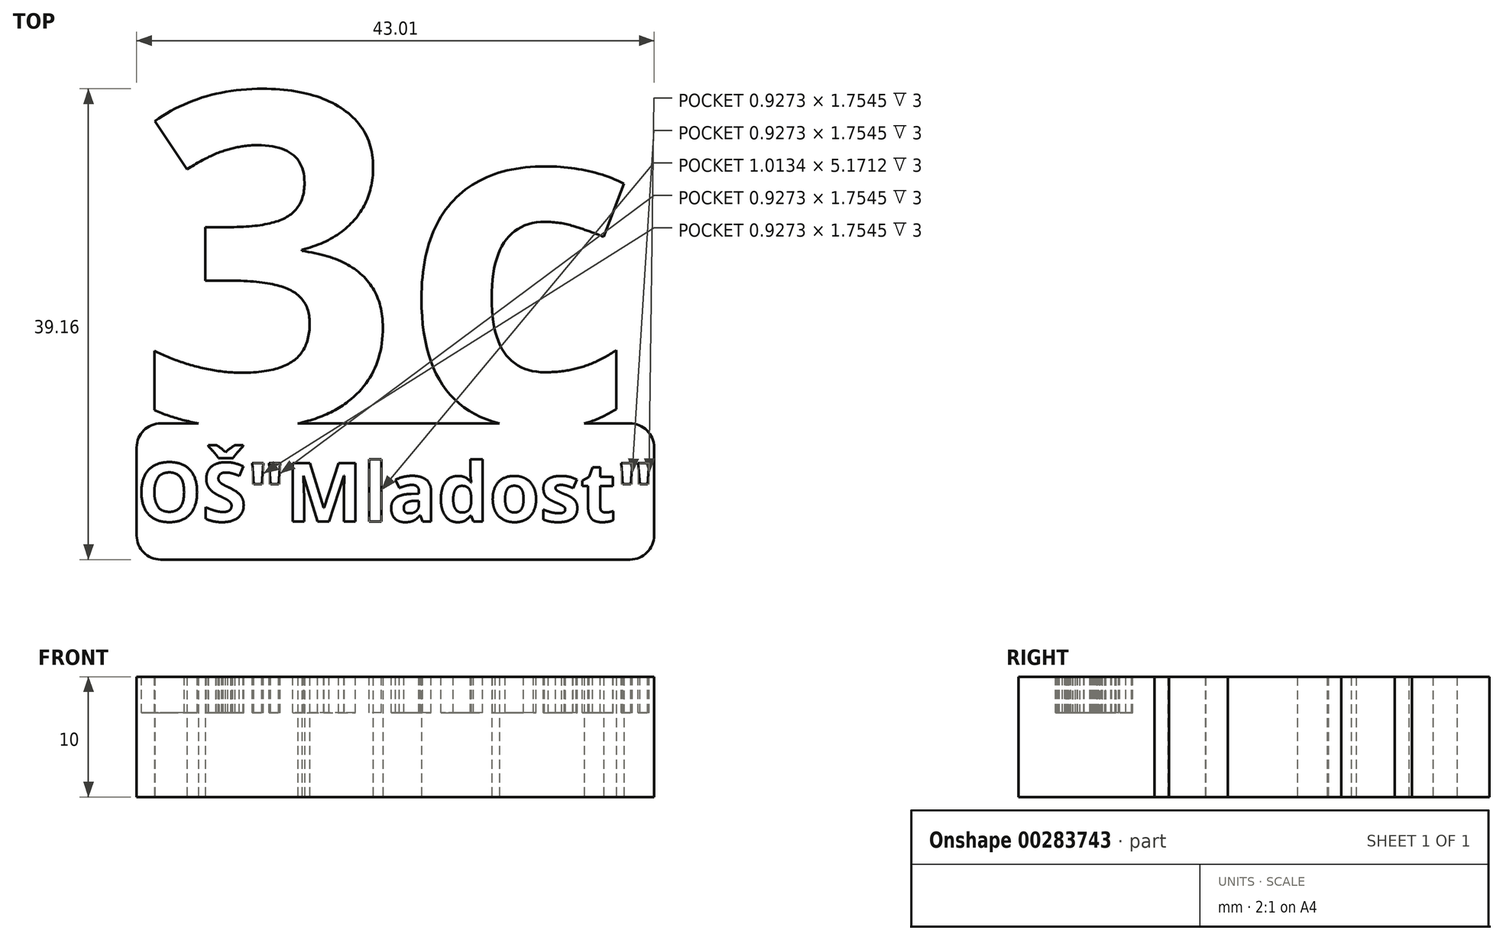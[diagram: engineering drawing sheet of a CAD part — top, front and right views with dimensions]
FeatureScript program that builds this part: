
annotation { "Feature Type Name" : "Feature", "Feature Type Description" : "" }
export const myFeature = defineFeature(function(context is Context, id is Id, definition is map)
    precondition{}
    {
        {
            var Q0;
            Q0=qCreatedBy(makeId("Top.planeOp"),FACE);
            var sketch = newSketch(context, id + "F0", { "sketchPlane" : qUnion([Q0])});
            skText(sketch, "E0", { "text": "3c", "fontName": "OpenSans-Bold.ttf"});
            skLineSegment(sketch, "E1.bottom", {"start": v(0, 0) * mm, "end": v(43, 0) * mm});
            skLineSegment(sketch, "E1.top", {"start": v(0, -11.32) * mm, "end": v(43, -11.32) * mm});
            skLineSegment(sketch, "E1.left", {"start": v(0, 0) * mm, "end": v(0, -11.32) * mm});
            skLineSegment(sketch, "E1.right", {"start": v(43, 0) * mm, "end": v(43, -11.32) * mm});
            const initialGuessF0  = {"E0": [0, 0, 1, 0, 0.02768]};
            skSetInitialGuess(sketch, initialGuessF0);
            skSolve(sketch);
        }
        {
            var Q0;
            Q0 = qSketchRegion(id + "F0", true);
            extrude(context, id + "F1", {"entities" : qUnion([Q0]), "depth" : 10 * mm});
        }
        {
            var Q0;
            Q0=makeQuery(id+"F1.opExtrude","CAP_FACE",FACE,{"disambiguationData":[OSD([sQuery(id+"F0.wireOp",EDGE,"E0.sketch_text.stroke-0"),sQuery(id+"F0.wireOp",EDGE,"E0.sketch_text.stroke-1"),sQuery(id+"F0.wireOp",EDGE,"E0.sketch_text.stroke-2"),sQuery(id+"F0.wireOp",EDGE,"E0.sketch_text.stroke-3"),sQuery(id+"F0.wireOp",EDGE,"E0.sketch_text.stroke-4"),sQuery(id+"F0.wireOp",EDGE,"E0.sketch_text.stroke-5"),sQuery(id+"F0.wireOp",EDGE,"E0.sketch_text.stroke-6"),sQuery(id+"F0.wireOp",EDGE,"E0.sketch_text.stroke-7"),sQuery(id+"F0.wireOp",EDGE,"E0.sketch_text.stroke-8"),sQuery(id+"F0.wireOp",EDGE,"E0.sketch_text.stroke-9"),sQuery(id+"F0.wireOp",EDGE,"E0.sketch_text.stroke-10"),sQuery(id+"F0.wireOp",EDGE,"E0.sketch_text.stroke-11"),sQuery(id+"F0.wireOp",EDGE,"E0.sketch_text.stroke-12"),sQuery(id+"F0.wireOp",EDGE,"E0.sketch_text.stroke-13"),sQuery(id+"F0.wireOp",EDGE,"E0.sketch_text.stroke-14"),sQuery(id+"F0.wireOp",EDGE,"E0.sketch_text.stroke-15"),sQuery(id+"F0.wireOp",EDGE,"E0.sketch_text.stroke-16"),sQuery(id+"F0.wireOp",EDGE,"E0.sketch_text.stroke-17"),sQuery(id+"F0.wireOp",EDGE,"E0.sketch_text.stroke-18"),sQuery(id+"F0.wireOp",EDGE,"E0.sketch_text.stroke-19"),sQuery(id+"F0.wireOp",EDGE,"E0.sketch_text.stroke-20"),sQuery(id+"F0.wireOp",EDGE,"E0.sketch_text.stroke-21"),sQuery(id+"F0.wireOp",EDGE,"E0.sketch_text.stroke-22"),sQuery(id+"F0.wireOp",EDGE,"E0.sketch_text.stroke-23"),sQuery(id+"F0.wireOp",EDGE,"E0.sketch_text.stroke-24"),sQuery(id+"F0.wireOp",EDGE,"E0.sketch_text.stroke-25"),sQuery(id+"F0.wireOp",EDGE,"E0.sketch_text.stroke-26"),sQuery(id+"F0.wireOp",EDGE,"E0.sketch_text.stroke-27"),sQuery(id+"F0.wireOp",EDGE,"E0.sketch_text.stroke-28"),sQuery(id+"F0.wireOp",EDGE,"E0.sketch_text.stroke-29"),sQuery(id+"F0.wireOp",EDGE,"E0.sketch_text.stroke-30"),sQuery(id+"F0.wireOp",EDGE,"E0.sketch_text.stroke-31"),sQuery(id+"F0.wireOp",EDGE,"E0.sketch_text.stroke-32"),sQuery(id+"F0.wireOp",EDGE,"E0.sketch_text.stroke-33"),sQuery(id+"F0.wireOp",EDGE,"E0.sketch_text.stroke-34"),sQuery(id+"F0.wireOp",EDGE,"E0.sketch_text.stroke-35"),sQuery(id+"F0.wireOp",EDGE,"E0.sketch_text.stroke-36"),sQuery(id+"F0.wireOp",EDGE,"E0.sketch_text.stroke-37"),sQuery(id+"F0.wireOp",EDGE,"E0.sketch_text.stroke-38"),sQuery(id+"F0.wireOp",EDGE,"E0.sketch_text.stroke-39"),sQuery(id+"F0.wireOp",EDGE,"E1.bottom"),sQuery(id+"F0.wireOp",EDGE,"E1.top"),sQuery(id+"F0.wireOp",EDGE,"E1.left"),sQuery(id+"F0.wireOp",EDGE,"E1.right")])],"isStart":false});
            var sketch = newSketch(context, id + "F2", { "sketchPlane" : qUnion([Q0])});
            skText(sketch, "E2", { "text": "OŠ\"Mladost\"", "fontName": "OpenSans-Bold.ttf"});
            const initialGuessF2  = {"E2": [0, -0.00815, 1, 0, 0.0049]};
            skSetInitialGuess(sketch, initialGuessF2);
            skSolve(sketch);
        }
        {
            var Q0;
            Q0 = qSketchRegion(id + "F2", true);
            extrude(context, id + "F3", {"entities" : qUnion([Q0]), "operationType" : NewBodyOperationType.REMOVE, "oppositeDirection" : true, "depth" : 3 * mm});
        }
        {
            var Q0;
            Q0=makeQuery(id+"F1.opExtrude","SWEPT_EDGE",EDGE,{"disambiguationData":[OSD([sQuery(id+"F0.wireOp",EDGE,"E1.top"),sQuery(id+"F0.wireOp",EDGE,"E1.right")])]});
            var Q1;
            Q1=makeQuery(id+"F1.opExtrude","SWEPT_EDGE",EDGE,{"disambiguationData":[OSD([sQuery(id+"F0.wireOp",EDGE,"E1.top"),sQuery(id+"F0.wireOp",EDGE,"E1.left")])]});
            var Q2;
            Q2=makeQuery(id+"F1.opExtrude","SWEPT_EDGE",EDGE,{"disambiguationData":[OSD([sQuery(id+"F0.wireOp",EDGE,"E1.bottom"),sQuery(id+"F0.wireOp",EDGE,"E1.left")])]});
            var Q3;
            Q3=makeQuery(id+"F1.opExtrude","SWEPT_EDGE",EDGE,{"disambiguationData":[OSD([sQuery(id+"F0.wireOp",EDGE,"E1.bottom"),sQuery(id+"F0.wireOp",EDGE,"E1.right")])]});
            fillet(context, id + "F4", {"entities" : qUnion([Q0, Q1, Q2, Q3]), "radius" : 2 * mm, "tangentPropagation" : true, "allowEdgeOverflow" : false});
        }
    });
